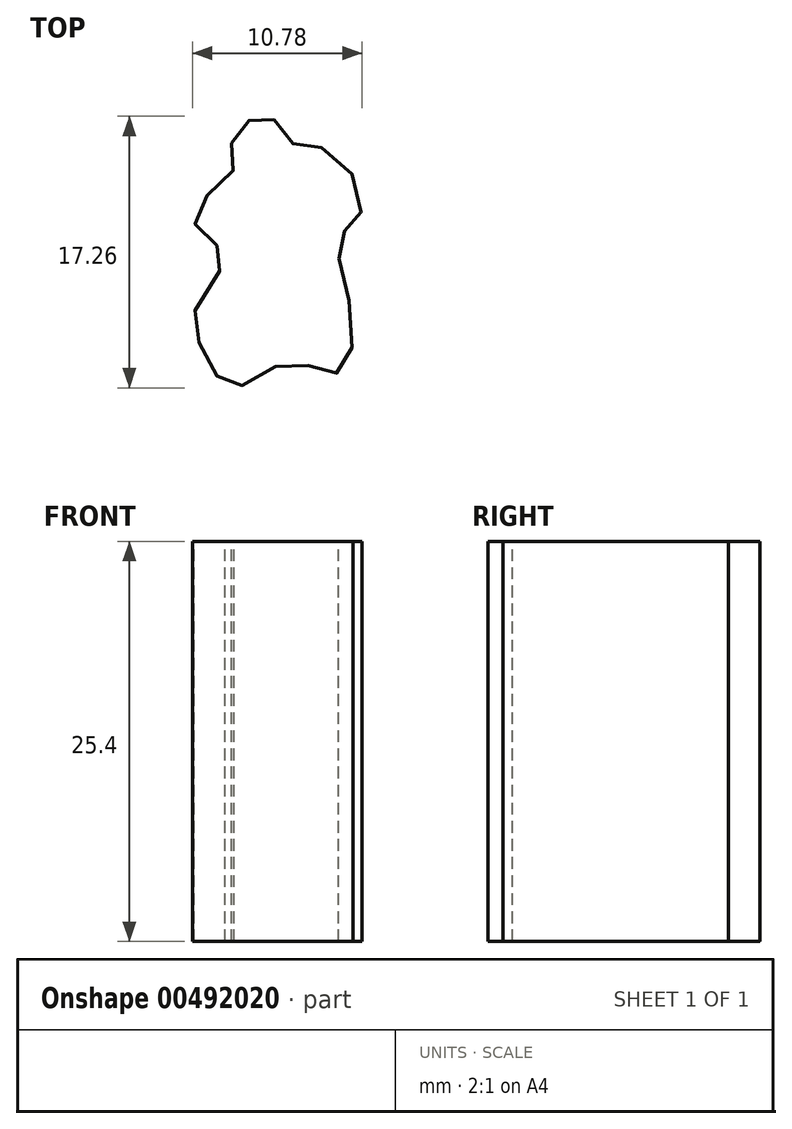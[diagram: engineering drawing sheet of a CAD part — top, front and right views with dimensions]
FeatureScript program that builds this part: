
annotation { "Feature Type Name" : "Feature", "Feature Type Description" : "" }
export const myFeature = defineFeature(function(context is Context, id is Id, definition is map)
    precondition{}
    {
        {
            var Q0;
            Q0=qCreatedBy(makeId("Top.planeOp"),FACE);
            var sketch = newSketch(context, id + "F0", { "sketchPlane" : qUnion([Q0])});
            skFitSpline(sketch, "E0", {"points": [v(0, 10.83) * mm, v(-1.5, 10.83) * mm, v(-2.68, 9.34) * mm, v(-2.6, 7.55) * mm, v(-4.87, 5.32) * mm, v(-4.53, 3.46) * mm, v(-3.1, 2.17) * mm, v(-5.1, -1.5) * mm, v(-4.4, -4) * mm, v(-2.76, -6.19) * mm, v(0, -4.88) * mm, v(2.44, -4.88) * mm, v(4.25, -5.16) * mm, v(4.96, -1.85) * mm, v(4.1, 2.48) * mm, v(4.7, 4.04) * mm, v(5.6, 5.24) * mm, v(3.62, 8.87) * mm, v(1.38, 9.2) * mm, v(0, 10.83) * mm]});
            skSolve(sketch);
        }
        {
            var Q0;
            Q0=sQuery(id+"F0.wireOp",EDGE,"E0");
            extrude(context, id + "F1", {"bodyType" : ToolBodyType.SURFACE, "surfaceEntities" : qUnion([Q0]), "depth" : 25.4 * mm});
        }
    });
